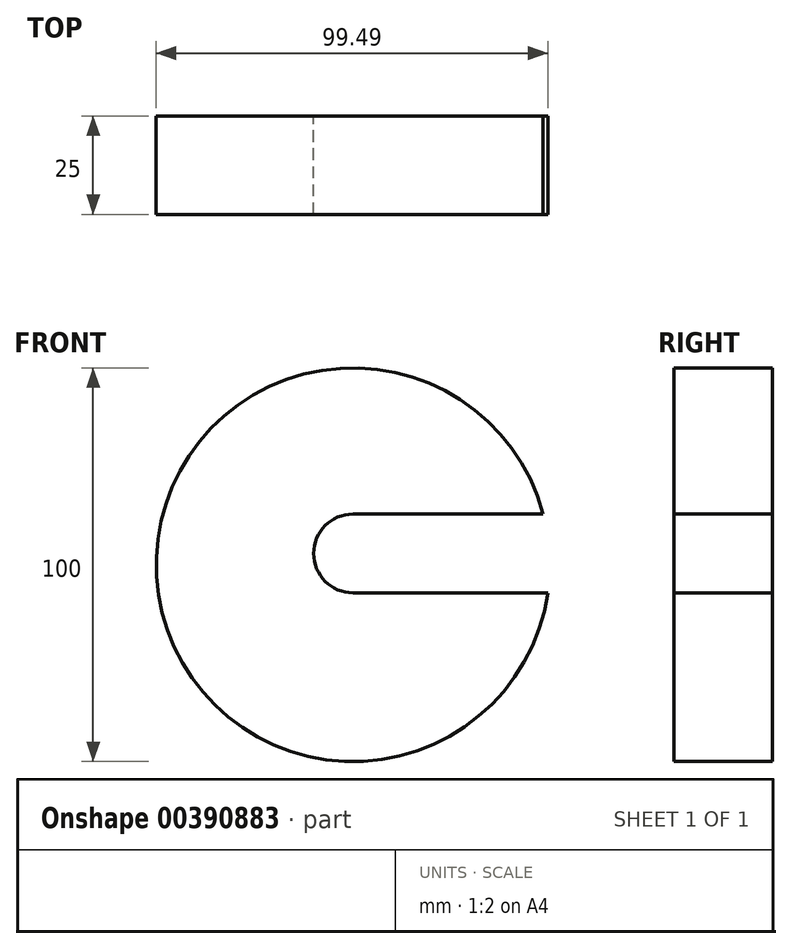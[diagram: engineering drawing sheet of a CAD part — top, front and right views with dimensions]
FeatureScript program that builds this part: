
annotation { "Feature Type Name" : "Feature", "Feature Type Description" : "" }
export const myFeature = defineFeature(function(context is Context, id is Id, definition is map)
    precondition{}
    {
        {
            var Q0;
            Q0=qCreatedBy(makeId("Front.planeOp"),FACE);
            var sketch = newSketch(context, id + "F0", { "sketchPlane" : qUnion([Q0])});
            skArc(sketch, "E0", {"start": v(48.32, 10) * mm, "mid": v(-49.91, -5.79) * mm, "end": v(49.49, -10) * mm});
            skLineSegment(sketch, "E1.bottom", {"start": v(0, 10) * mm, "end": v(48.32, 10) * mm});
            skLineSegment(sketch, "E1.top", {"start": v(0, -10) * mm, "end": v(49.49, -10) * mm});
            skArc(sketch, "E2", {"start": v(0, 10) * mm, "mid": v(-10, 0) * mm, "end": v(0, -10) * mm});
            skSolve(sketch);
        }
        {
            var Q0;
            Q0=makeQuery(id+"F0.imprint","IMPRINT",FACE,{"disambiguationData":[TD([[makeQuery(id+"F0.imprint","IMPRINT",EDGE,{"derivedFrom":sQuery(id+"F0.wireOp",EDGE,"E0")}),1.0]])]});
            extrude(context, id + "F1", {"entities" : qUnion([Q0]), "depth" : 25 * mm});
        }
    });
